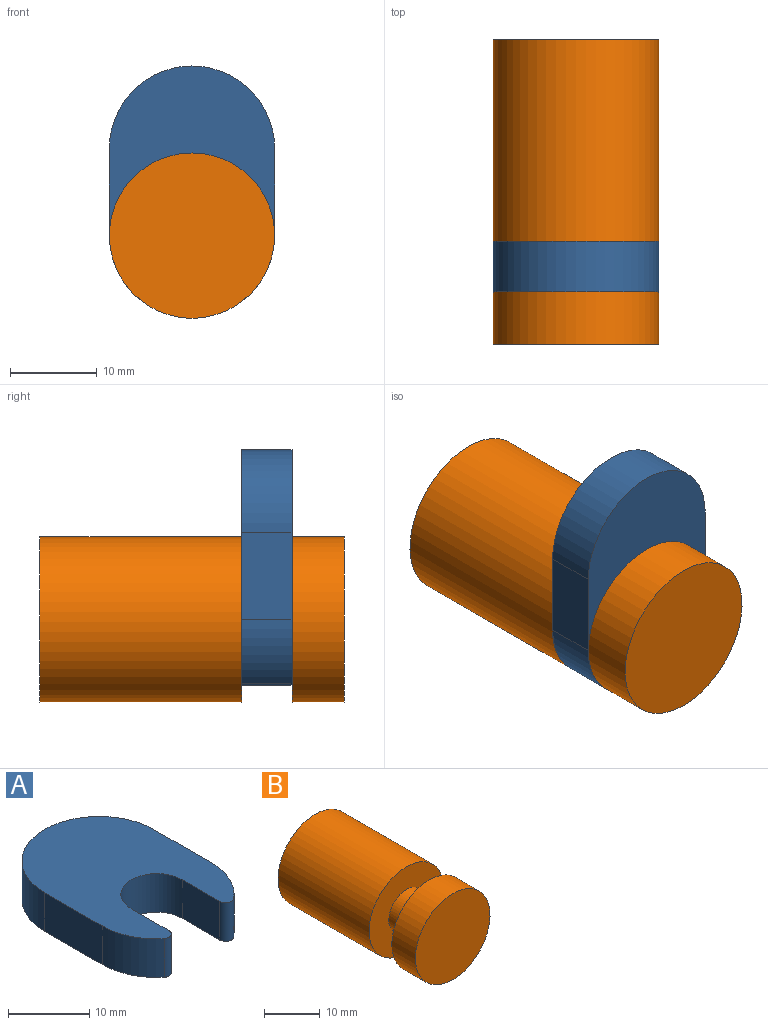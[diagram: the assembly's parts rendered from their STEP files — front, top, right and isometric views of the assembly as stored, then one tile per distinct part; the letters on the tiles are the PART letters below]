
ASSEMBLY  parts=2 mates=1
PART A: 12 faces, bbox 19x27.1x5.8 mm
  f0: cylinder r=9.5mm len=7.34mm, axis (0,0,-1), area 48.6mm2, adj f1,f8,f9,f11
  f1: plane 10x5.8mm, normal (1,0,0), area 58mm2, adj f0,f2,f8,f9
  f2: cylinder r=9.5mm len=19mm, axis (0,0,-1), area 173.1mm2, adj f1,f3,f8,f9
  f3: plane 10x5.8mm, normal (-1,0,0), area 58mm2, adj f2,f4,f8,f9
  f4: cylinder r=9.5mm len=7.34mm, axis (0,0,-1), area 48.6mm2, adj f3,f8,f9,f10
  f5: plane 6.56x5.8mm, normal (1,0,0), area 38.1mm2, adj f6,f8,f9,f10
  f6: cylinder r=4.4mm len=8.8mm, axis (0,0,-1), area 80.2mm2, adj f5,f7,f8,f9
  f7: plane 6.56x5.8mm, normal (-1,0,0), area 38.1mm2, adj f6,f8,f9,f11
  f8: plane 27.06x19mm, normal (0,0,1), area 360.9mm2, adj f0,f1,f2,f3,f4,f5,f6,f7
  f9: plane 27.06x19mm, normal (0,0,-1), area 360.9mm2, adj f0,f1,f2,f3,f4,f5,f6,f7
  f10: cylinder r=1mm len=5.8mm, axis (0,0,-1), area 13.1mm2, adj f4,f5,f8,f9
  f11: cylinder r=1mm len=5.8mm, axis (0,0,-1), area 13.1mm2, adj f0,f7,f8,f9
PART B: 7 faces, bbox 19x35x19 mm
  f0: plane 19x19mm, normal (0,-1,0), area 283.5mm2, adj f6
  f1: plane 19x19mm, normal (0,1,0), area 283.5mm2, adj f2
  f2: cylinder r=9.5mm len=23.2mm, axis (0,1,0), area 1384.8mm2, adj f1,f3
  f3: plane 19x19mm, normal (0,-1,0), area 219.9mm2, adj f2,f4
  f4: cylinder r=4.5mm len=9mm, axis (0,1,0), area 164mm2, adj f3,f5
  f5: plane 19x19mm, normal (0,1,0), area 219.9mm2, adj f4,f6
  f6: cylinder r=9.5mm len=19mm, axis (0,1,0), area 358.1mm2, adj f0,f5
PLACE A rot(axis=(0,0.71,0.71),180deg) t=(0,6,0)mm
PLACE B at identity fixed
MATE revolute A.f6 <-> B.f2  axis (0,-1,0) through (0,6,0)mm
